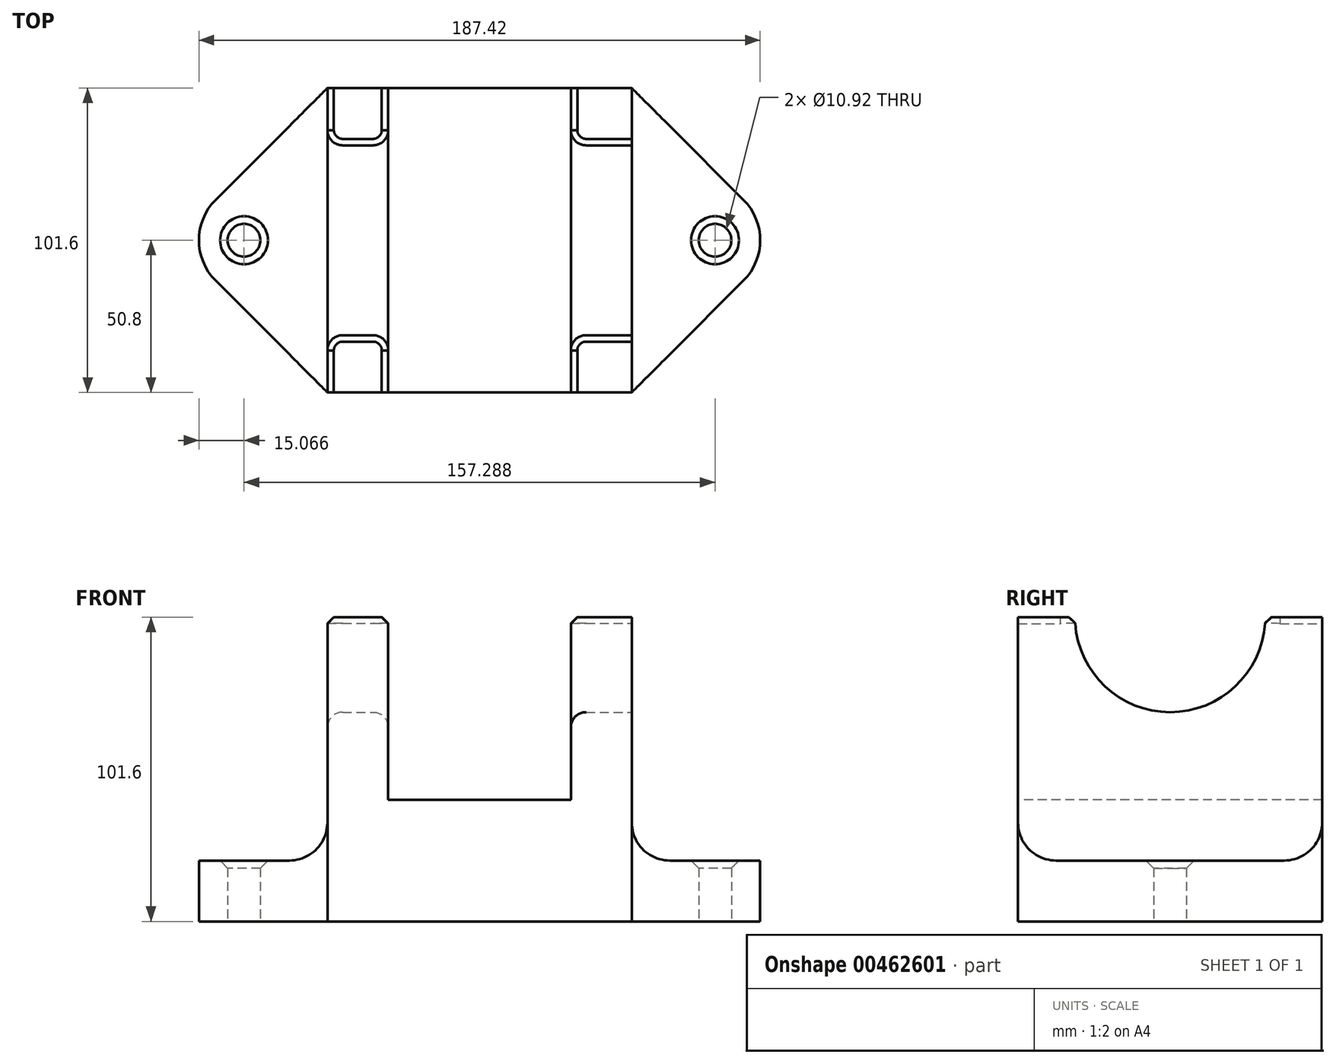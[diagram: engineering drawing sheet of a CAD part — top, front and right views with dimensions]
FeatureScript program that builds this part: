
annotation { "Feature Type Name" : "Feature", "Feature Type Description" : "" }
export const myFeature = defineFeature(function(context is Context, id is Id, definition is map)
    precondition{}
    {
        {
            var Q0;
            Q0=qCreatedBy(makeId("Top.planeOp"),FACE);
            var sketch = newSketch(context, id + "F0", { "sketchPlane" : qUnion([Q0])});
            skLineSegment(sketch, "E0.bottom", {"start": v(50.8, -50.8) * mm, "end": v(-50.8, -50.8) * mm});
            skLineSegment(sketch, "E0.top", {"start": v(50.8, 50.8) * mm, "end": v(-50.8, 50.8) * mm});
            skLineSegment(sketch, "E0.left", {"start": v(50.8, -50.8) * mm, "end": v(50.8, 50.8) * mm});
            skLineSegment(sketch, "E0.right", {"start": v(-50.8, -50.8) * mm, "end": v(-50.8, 50.8) * mm});
            skPoint(sketch, "E0.middle", {"position": v(0, 0) * mm});
            skLineSegment(sketch, "E1", {"start": v(50.8, 50.8) * mm, "end": v(101.6, 0) * mm});
            skLineSegment(sketch, "E2", {"start": v(50.8, -50.8) * mm, "end": v(101.6, 0) * mm});
            skLineSegment(sketch, "E3", {"start": v(-50.8, 50.8) * mm, "end": v(-101.6, 0) * mm});
            skLineSegment(sketch, "E4", {"start": v(-101.6, 0) * mm, "end": v(-50.8, -50.8) * mm});
            skLineSegment(sketch, "E5", {"start": v(0, 50.8) * mm, "end": v(0, -50.8) * mm, "construction": true});
            skCircle(sketch, "E6", {"center": v(78.64, 0) * mm, "radius": 5.46 * mm});
            skCircle(sketch, "E7.MirrorC", {"center": v(-78.64, 0) * mm, "radius": 5.46 * mm});
            skSolve(sketch);
        }
        {
            var Q0;
            Q0=makeQuery(id+"F0.imprint","IMPRINT",FACE,{"disambiguationData":[TD([[makeQuery(id+"F0.imprint","IMPRINT",EDGE,{"derivedFrom":sQuery(id+"F0.wireOp",EDGE,"E0.bottom")}),-1.0]])]});
            var Q1;
            Q1=makeQuery(id+"F0.imprint","IMPRINT",FACE,{"disambiguationData":[TD([[makeQuery(id+"F0.imprint","IMPRINT",EDGE,{"derivedFrom":sQuery(id+"F0.wireOp",EDGE,"E0.right")}),1.0]])]});
            var Q2;
            Q2=makeQuery(id+"F0.imprint","IMPRINT",FACE,{"disambiguationData":[TD([[makeQuery(id+"F0.imprint","IMPRINT",EDGE,{"derivedFrom":sQuery(id+"F0.wireOp",EDGE,"E0.left")}),-1.0]])]});
            extrude(context, id + "F1", {"entities" : qUnion([Q0, Q1, Q2]), "depth" : 20.32 * mm});
        }
        {
            var Q0;
            Q0=makeQuery(id+"F1.opExtrude","SWEPT_EDGE",EDGE,{"disambiguationData":[OSD([sQuery(id+"F0.wireOp",EDGE,"E1"),sQuery(id+"F0.wireOp",EDGE,"E2")])]});
            var Q1;
            Q1=makeQuery(id+"F1.opExtrude","SWEPT_EDGE",EDGE,{"disambiguationData":[OSD([sQuery(id+"F0.wireOp",EDGE,"E3"),sQuery(id+"F0.wireOp",EDGE,"E4")])]});
            fillet(context, id + "F2", {"entities" : qUnion([Q0, Q1]), "radius" : 19.05 * mm, "tangentPropagation" : true, "allowEdgeOverflow" : false});
        }
        {
            var Q0;
            Q0=makeQuery(id+"F0.imprint","IMPRINT",FACE,{"disambiguationData":[TD([[makeQuery(id+"F0.imprint","IMPRINT",EDGE,{"derivedFrom":sQuery(id+"F0.wireOp",EDGE,"E0.bottom")}),-1.0]])]});
            extrude(context, id + "F3", {"entities" : qUnion([Q0]), "operationType" : NewBodyOperationType.ADD, "depth" : 40.64 * mm});
        }
        {
            var Q0;
            Q0=makeQuery(id+"F3.opExtrude","CAP_FACE",FACE,{"disambiguationData":[OSD([sQuery(id+"F0.wireOp",EDGE,"E0.bottom"),sQuery(id+"F0.wireOp",EDGE,"E0.top"),sQuery(id+"F0.wireOp",EDGE,"E0.left"),sQuery(id+"F0.wireOp",EDGE,"E0.right")])],"isStart":false});
            var sketch = newSketch(context, id + "F4", { "sketchPlane" : qUnion([Q0])});
            skLineSegment(sketch, "E8.bottom", {"start": v(-50.8, 50.8) * mm, "end": v(-30.48, 50.8) * mm});
            skLineSegment(sketch, "E8.top", {"start": v(-50.8, -50.8) * mm, "end": v(-30.48, -50.8) * mm});
            skLineSegment(sketch, "E8.left", {"start": v(-50.8, 50.8) * mm, "end": v(-50.8, -50.8) * mm});
            skLineSegment(sketch, "E8.right", {"start": v(-30.48, 50.8) * mm, "end": v(-30.48, -50.8) * mm});
            skLineSegment(sketch, "E9.MirrorCS", {"start": v(50.8, 50.8) * mm, "end": v(50.8, -50.8) * mm});
            skLineSegment(sketch, "E10.MirrorCS", {"start": v(50.8, 50.8) * mm, "end": v(30.48, 50.8) * mm});
            skLineSegment(sketch, "E11.MirrorCS", {"start": v(30.48, 50.8) * mm, "end": v(30.48, -50.8) * mm});
            skLineSegment(sketch, "E12.MirrorCS", {"start": v(50.8, -50.8) * mm, "end": v(30.48, -50.8) * mm});
            skSolve(sketch);
        }
        {
            var Q0;
            Q0=makeQuery(id+"F4.imprint","IMPRINT",FACE,{"disambiguationData":[TD([[makeQuery(id+"F4.imprint","IMPRINT",EDGE,{"derivedFrom":sQuery(id+"F4.wireOp",EDGE,"E9.MirrorCS")}),1.0]])]});
            var Q1;
            Q1=makeQuery(id+"F4.imprint","IMPRINT",FACE,{"disambiguationData":[TD([[makeQuery(id+"F4.imprint","IMPRINT",EDGE,{"derivedFrom":sQuery(id+"F4.wireOp",EDGE,"E8.bottom")}),1.0]])]});
            extrude(context, id + "F5", {"entities" : qUnion([Q0, Q1]), "operationType" : NewBodyOperationType.ADD, "depth" : 60.96 * mm});
        }
        {
            var Q0;
            Q0=makeQuery(id+"F5.boolean.opBoolean","MERGE",FACE,{"derivedFrom":[makeQuery(id+"F3.opExtrude","SWEPT_FACE",FACE,{"disambiguationData":[OSD([sQuery(id+"F0.wireOp",EDGE,"E0.left")])]}),makeQuery(id+"F5.opExtrude","SWEPT_FACE",FACE,{"disambiguationData":[OSD([sQuery(id+"F4.wireOp",EDGE,"E9.MirrorCS")])]})]});
            var sketch = newSketch(context, id + "F6", { "sketchPlane" : qUnion([Q0])});
            skCircle(sketch, "E13", {"center": v(0, 101.6) * mm, "radius": 31.75 * mm});
            skSolve(sketch);
        }
        {
            var Q0;
            Q0 = qSketchRegion(id + "F6", true);
            extrude(context, id + "F7", {"entities" : qUnion([Q0]), "operationType" : NewBodyOperationType.REMOVE, "endBound" : BoundingType.THROUGH_ALL, "oppositeDirection" : true, "depth" : 25.4 * mm});
        }
        {
            var Q0;
            Q0=makeQuery(id+"F0.imprint","IMPRINT",FACE,{"disambiguationData":[TD([[makeQuery(id+"F0.imprint","IMPRINT",EDGE,{"derivedFrom":sQuery(id+"F0.wireOp",EDGE,"E6")}),1.0]])]});
            var Q1;
            Q1=makeQuery(id+"F0.imprint","IMPRINT",FACE,{"disambiguationData":[TD([[makeQuery(id+"F0.imprint","IMPRINT",EDGE,{"derivedFrom":sQuery(id+"F0.wireOp",EDGE,"E7.MirrorC")}),-1.0]])]});
            var Q2;
            Q2 = qSketchRegion(id + "F0", true);
            extrude(context, id + "F8", {"entities" : qUnion([Q0, Q1, Q2]), "operationType" : NewBodyOperationType.REMOVE, "endBound" : BoundingType.THROUGH_ALL, "oppositeDirection" : true, "depth" : 25.4 * mm});
        }
        {
            var Q0;
            Q0=makeQuery(id+"F7.boolean.opBoolean","COPY",EDGE,{"derivedFrom":makeQuery(id+"F7.opExtrude","CAP_EDGE",EDGE,{"disambiguationData":[OSD([sQuery(id+"F6.wireOp",EDGE,"E13")])],"isStart":true})});
            var Q1;
            Q1=makeQuery(id+"F7.boolean.opBoolean","INTERSECT",EDGE,{"derivedFrom":[makeQuery(id+"F5.opExtrude","SWEPT_FACE",FACE,{"disambiguationData":[OSD([sQuery(id+"F4.wireOp",EDGE,"E11.MirrorCS")])]}),makeQuery(id+"F7.opExtrude","SWEPT_FACE",FACE,{"disambiguationData":[OSD([sQuery(id+"F6.wireOp",EDGE,"E13")])]})]});
            var Q2;
            Q2=makeQuery(id+"F7.boolean.opBoolean","INTERSECT",EDGE,{"derivedFrom":[makeQuery(id+"F5.boolean.opBoolean","MERGE",FACE,{"derivedFrom":[makeQuery(id+"F3.opExtrude","SWEPT_FACE",FACE,{"disambiguationData":[OSD([sQuery(id+"F0.wireOp",EDGE,"E0.right")])]}),makeQuery(id+"F5.opExtrude","SWEPT_FACE",FACE,{"disambiguationData":[OSD([sQuery(id+"F4.wireOp",EDGE,"E8.left")])]})]}),makeQuery(id+"F7.opExtrude","SWEPT_FACE",FACE,{"disambiguationData":[OSD([sQuery(id+"F6.wireOp",EDGE,"E13")])]})]});
            var Q3;
            Q3=makeQuery(id+"F7.boolean.opBoolean","INTERSECT",EDGE,{"derivedFrom":[makeQuery(id+"F5.opExtrude","SWEPT_FACE",FACE,{"disambiguationData":[OSD([sQuery(id+"F4.wireOp",EDGE,"E8.right")])]}),makeQuery(id+"F7.opExtrude","SWEPT_FACE",FACE,{"disambiguationData":[OSD([sQuery(id+"F6.wireOp",EDGE,"E13")])]})]});
            fillet(context, id + "F9", {"entities" : qUnion([Q0, Q1, Q2, Q3]), "radius" : 5.08 * mm, "tangentPropagation" : true, "allowEdgeOverflow" : false});
        }
        {
            var Q0;
            {var subQ0=sQuery(id+"F4.wireOp",EDGE,"E8.top");var subQ1=makeQuery(id+"F3.opExtrude","SWEPT_FACE",FACE,{"disambiguationData":[OSD([sQuery(id+"F0.wireOp",EDGE,"E0.right")])]});var subQ2=sQuery(id+"F0.wireOp",EDGE,"E0.bottom");var subQ3=sQuery(id+"F4.wireOp",EDGE,"E8.left");var subQ4=makeQuery(id+"F5.opExtrude","SWEPT_FACE",FACE,{"disambiguationData":[OSD([subQ3])]});var subQ5=sQuery(id+"F4.wireOp",EDGE,"E8.right");var subQ6=makeQuery(id+"F7.opExtrude","SWEPT_FACE",FACE,{"disambiguationData":[OSD([sQuery(id+"F6.wireOp",EDGE,"E13")])]});Q0=makeQuery(id+"F9.opFillet","BLEND_EDGE",EDGE,{"blendedFrom":[makeQuery(id+"F7.boolean.opBoolean","INTERSECT",EDGE,{"derivedFrom":[makeQuery(id+"F5.boolean.opBoolean","MERGE",FACE,{"derivedFrom":[subQ1,subQ4]}),subQ6]}),makeQuery(id+"F7.boolean.opBoolean","SPLIT",FACE,{"disambiguationData":[TD([makeQuery(id+"F1.opExtrude","SWEPT_FACE",FACE,{"disambiguationData":[OSD([subQ2])]})])],"derivedFrom":makeQuery(id+"F5.opExtrude","CAP_FACE",FACE,{"disambiguationData":[OSD([sQuery(id+"F4.wireOp",EDGE,"E8.bottom"),subQ0,subQ3,subQ5])],"isStart":false})})],"blendedInto":[makeQuery(id+"F7.boolean.opBoolean","SPLIT",FACE,{"disambiguationData":[TD([makeQuery(id+"F1.opExtrude","SWEPT_FACE",FACE,{"disambiguationData":[OSD([subQ2])]})])],"derivedFrom":makeQuery(id+"F5.opExtrude","CAP_FACE",FACE,{"disambiguationData":[OSD([sQuery(id+"F4.wireOp",EDGE,"E8.bottom"),subQ0,subQ3,subQ5])],"isStart":false})})]});}
            var Q1;
            {var subQ0=sQuery(id+"F4.wireOp",EDGE,"E8.left");var subQ2=sQuery(id+"F0.wireOp",EDGE,"E0.bottom");Q1=makeQuery(id+"F7.boolean.opBoolean","SPLIT",EDGE,{"disambiguationData":[TD([makeQuery(id+"F1.opExtrude","SWEPT_FACE",FACE,{"disambiguationData":[OSD([subQ2])]})])],"derivedFrom":makeQuery(id+"F5.opExtrude","CAP_EDGE",EDGE,{"disambiguationData":[OSD([subQ0])],"isStart":false})});}
            var Q2;
            {var subQ1=sQuery(id+"F4.wireOp",EDGE,"E11.MirrorCS");var subQ2=sQuery(id+"F0.wireOp",EDGE,"E0.bottom");Q2=makeQuery(id+"F7.boolean.opBoolean","SPLIT",EDGE,{"disambiguationData":[TD([makeQuery(id+"F1.opExtrude","SWEPT_FACE",FACE,{"disambiguationData":[OSD([subQ2])]})])],"derivedFrom":makeQuery(id+"F5.opExtrude","CAP_EDGE",EDGE,{"disambiguationData":[OSD([subQ1])],"isStart":false})});}
            var Q3;
            Q3=makeQuery(id+"F7.boolean.opBoolean","INTERSECT",EDGE,{"disambiguationData":[OD(0.0)],"derivedFrom":[makeQuery(id+"F5.opExtrude","CAP_FACE",FACE,{"disambiguationData":[OSD([sQuery(id+"F4.wireOp",EDGE,"E8.bottom"),sQuery(id+"F4.wireOp",EDGE,"E8.top"),sQuery(id+"F4.wireOp",EDGE,"E8.left"),sQuery(id+"F4.wireOp",EDGE,"E8.right")])],"isStart":false}),makeQuery(id+"F7.opExtrude","SWEPT_FACE",FACE,{"disambiguationData":[OSD([sQuery(id+"F6.wireOp",EDGE,"E13")])]})]});
            var Q4;
            Q4=makeQuery(id+"F7.boolean.opBoolean","INTERSECT",EDGE,{"disambiguationData":[OD(0.0)],"derivedFrom":[makeQuery(id+"F5.opExtrude","CAP_FACE",FACE,{"disambiguationData":[OSD([sQuery(id+"F4.wireOp",EDGE,"E9.MirrorCS"),sQuery(id+"F4.wireOp",EDGE,"E10.MirrorCS"),sQuery(id+"F4.wireOp",EDGE,"E11.MirrorCS"),sQuery(id+"F4.wireOp",EDGE,"E12.MirrorCS")])],"isStart":false}),makeQuery(id+"F7.opExtrude","SWEPT_FACE",FACE,{"disambiguationData":[OSD([sQuery(id+"F6.wireOp",EDGE,"E13")])]})]});
            chamfer(context, id + "F10", {"entities" : qUnion([Q0, Q1, Q2, Q3, Q4]), "width" : 2.16 * mm, "tangentPropagation" : true});
        }
        {
            var Q0;
            Q0=makeQuery(id+"F3.boolean.opBoolean","INTERSECT",EDGE,{"derivedFrom":[makeQuery(id+"F1.opExtrude","CAP_FACE",FACE,{"disambiguationData":[OSD([sQuery(id+"F0.wireOp",EDGE,"E0.bottom"),sQuery(id+"F0.wireOp",EDGE,"E0.top"),sQuery(id+"F0.wireOp",EDGE,"E1"),sQuery(id+"F0.wireOp",EDGE,"E2"),sQuery(id+"F0.wireOp",EDGE,"E3"),sQuery(id+"F0.wireOp",EDGE,"E4"),sQuery(id+"F0.wireOp",EDGE,"E6"),sQuery(id+"F0.wireOp",EDGE,"E7.MirrorC")])],"isStart":false}),makeQuery(id+"F3.opExtrude","SWEPT_FACE",FACE,{"disambiguationData":[OSD([sQuery(id+"F0.wireOp",EDGE,"E0.left")])]})]});
            var Q1;
            Q1=makeQuery(id+"F5.opExtrude","CAP_EDGE",EDGE,{"disambiguationData":[OSD([sQuery(id+"F4.wireOp",EDGE,"E11.MirrorCS")])],"isStart":true});
            var Q2;
            Q2=makeQuery(id+"F5.opExtrude","CAP_EDGE",EDGE,{"disambiguationData":[OSD([sQuery(id+"F4.wireOp",EDGE,"E8.right")])],"isStart":true});
            var Q3;
            Q3=makeQuery(id+"F3.boolean.opBoolean","INTERSECT",EDGE,{"derivedFrom":[makeQuery(id+"F1.opExtrude","CAP_FACE",FACE,{"disambiguationData":[OSD([sQuery(id+"F0.wireOp",EDGE,"E0.bottom"),sQuery(id+"F0.wireOp",EDGE,"E0.top"),sQuery(id+"F0.wireOp",EDGE,"E1"),sQuery(id+"F0.wireOp",EDGE,"E2"),sQuery(id+"F0.wireOp",EDGE,"E3"),sQuery(id+"F0.wireOp",EDGE,"E4"),sQuery(id+"F0.wireOp",EDGE,"E6"),sQuery(id+"F0.wireOp",EDGE,"E7.MirrorC")])],"isStart":false}),makeQuery(id+"F3.opExtrude","SWEPT_FACE",FACE,{"disambiguationData":[OSD([sQuery(id+"F0.wireOp",EDGE,"E0.right")])]})]});
            fillet(context, id + "F11", {"entities" : qUnion([Q0, Q1, Q2, Q3]), "radius" : 12.7 * mm, "tangentPropagation" : true, "allowEdgeOverflow" : false});
        }
        {
            var Q0;
            Q0=makeQuery(id+"F1.opExtrude","CAP_EDGE",EDGE,{"disambiguationData":[OSD([sQuery(id+"F0.wireOp",EDGE,"E7.MirrorC")])],"isStart":false});
            var Q1;
            Q1=makeQuery(id+"F1.opExtrude","CAP_EDGE",EDGE,{"disambiguationData":[OSD([sQuery(id+"F0.wireOp",EDGE,"E6")])],"isStart":false});
            chamfer(context, id + "F12", {"entities" : qUnion([Q0, Q1]), "width" : 2.54 * mm, "tangentPropagation" : true});
        }
    });
